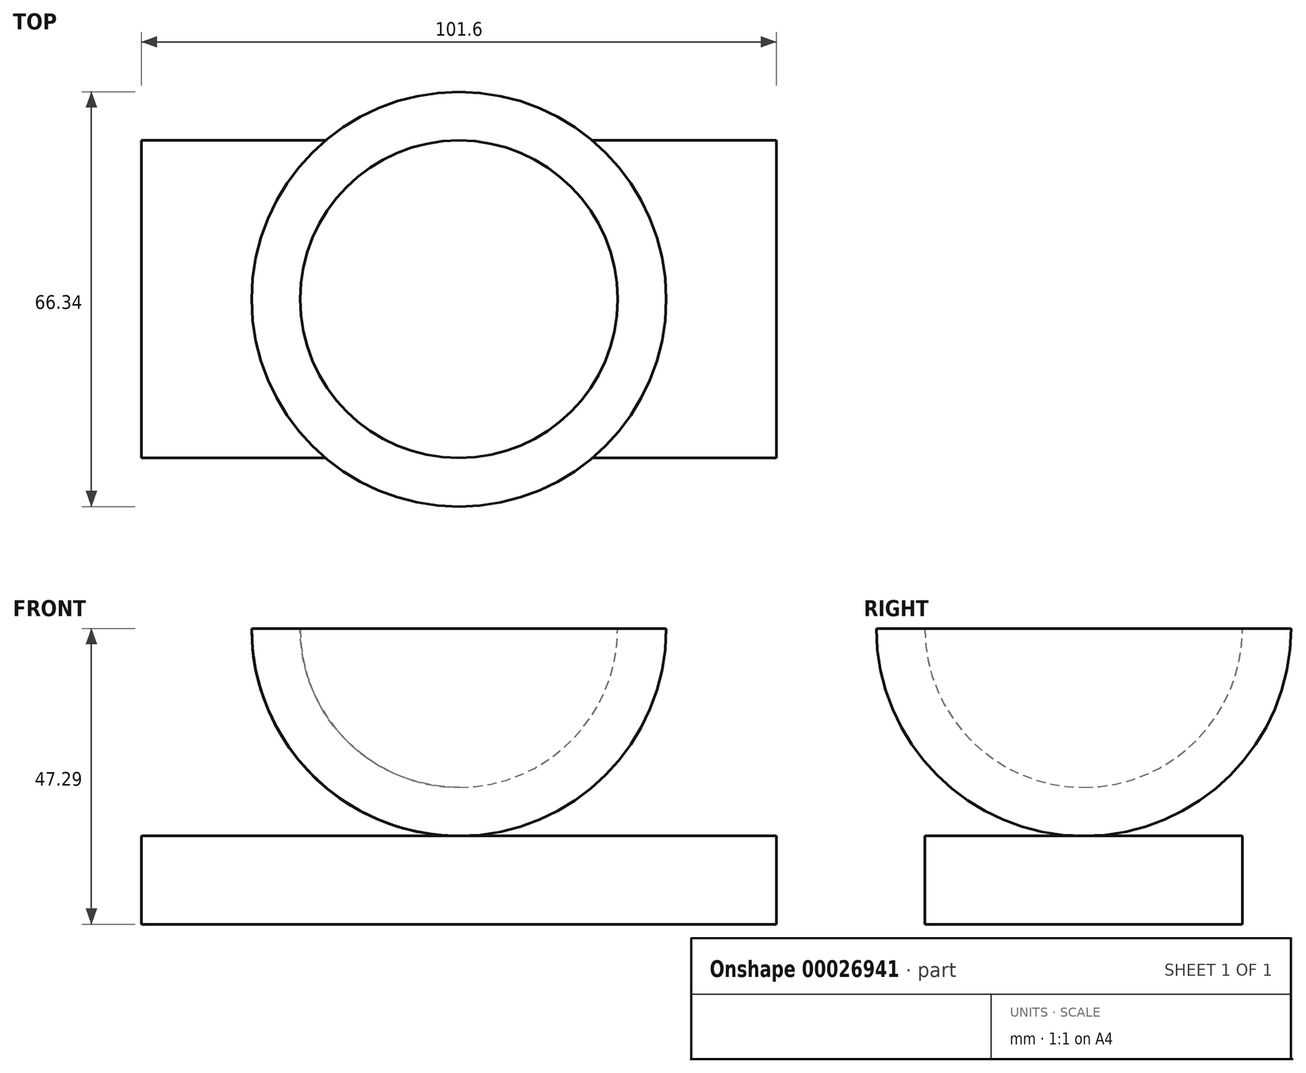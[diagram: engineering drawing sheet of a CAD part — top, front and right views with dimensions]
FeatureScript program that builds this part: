
annotation { "Feature Type Name" : "Feature", "Feature Type Description" : "" }
export const myFeature = defineFeature(function(context is Context, id is Id, definition is map)
    precondition{}
    {
        {
            var Q0;
            Q0=qCreatedBy(makeId("Front.planeOp"),FACE);
            var sketch = newSketch(context, id + "F0", { "sketchPlane" : qUnion([Q0])});
            skLineSegment(sketch, "E0", {"start": v(42.74, 22.2) * mm, "end": v(50.52, 22.2) * mm});
            skLineSegment(sketch, "E1", {"start": v(50.52, 22.2) * mm, "end": v(42.74, 22.2) * mm});
            skLineSegment(sketch, "E2", {"start": v(17.34, -10.97) * mm, "end": v(17.34, -25.09) * mm});
            skArc(sketch, "E3", {"start": v(-15.83, 22.2) * mm, "mid": v(17.34, -10.97) * mm, "end": v(50.52, 22.2) * mm});
            skArc(sketch, "E4", {"start": v(-8.06, 22.2) * mm, "mid": v(17.34, -3.2) * mm, "end": v(42.74, 22.2) * mm});
            skLineSegment(sketch, "E5.bottom", {"start": v(17.34, -25.09) * mm, "end": v(68.14, -25.09) * mm});
            skLineSegment(sketch, "E5.top", {"start": v(17.34, -10.97) * mm, "end": v(68.14, -10.97) * mm});
            skLineSegment(sketch, "E5.right", {"start": v(68.14, -10.97) * mm, "end": v(68.14, -25.09) * mm});
            skLineSegment(sketch, "E6.MirrorCS", {"start": v(17.34, -10.97) * mm, "end": v(-33.46, -10.97) * mm});
            skLineSegment(sketch, "E7.MirrorCS", {"start": v(-33.46, -10.97) * mm, "end": v(-33.46, -25.09) * mm});
            skLineSegment(sketch, "E8.MirrorCS", {"start": v(17.34, -25.09) * mm, "end": v(-33.46, -25.09) * mm});
            skLineSegment(sketch, "E9.trimOffspring", {"start": v(-8.06, 22.2) * mm, "end": v(-15.83, 22.2) * mm});
            skLineSegment(sketch, "E10", {"start": v(17.34, 22.2) * mm, "end": v(17.34, -25.09) * mm});
            skSolve(sketch);
        }
        {
            var Q0;
            {var subQ0=sQuery(id+"F0.wireOp",EDGE,"E9.trimOffspring");Q0=makeQuery(id+"F0.imprint","IMPRINT",FACE,{"disambiguationData":[TD([[makeQuery(id+"F0.imprint","IMPRINT",EDGE,{"derivedFrom":subQ0}),1.0]])]});}
            var Q1;
            {var subQ3=sQuery(id+"F0.wireOp",EDGE,"E2");Q1=makeQuery(id+"F0.imprint","IMPRINT",FACE,{"disambiguationData":[TD([[makeQuery(id+"F0.imprint","IMPRINT",EDGE,{"derivedFrom":subQ3}),-1.0]])]});}
            var Q2;
            Q2=sQuery(id+"F0.wireOp",EDGE,"E2");
            revolve(context, id + "F1", {"entities" : qUnion([Q0, Q1]), "axis" : qUnion([Q2]), "revolveType" : RevolveType.FULL});
        }
        {
            var Q0;
            {var subQ1=sQuery(id+"F0.wireOp",EDGE,"E6.MirrorCS");Q0=makeQuery(id+"F0.imprint","IMPRINT",FACE,{"disambiguationData":[TD([[makeQuery(id+"F0.imprint","IMPRINT",EDGE,{"derivedFrom":subQ1}),1.0]])]});}
            var Q1;
            {var subQ2=sQuery(id+"F0.wireOp",EDGE,"E5.bottom");Q1=makeQuery(id+"F0.imprint","IMPRINT",FACE,{"disambiguationData":[TD([[makeQuery(id+"F0.imprint","IMPRINT",EDGE,{"derivedFrom":subQ2}),1.0]])]});}
            extrude(context, id + "F2", {"entities" : qUnion([Q0, Q1]), "endBound" : BoundingType.SYMMETRIC, "depth" : 50.8 * mm});
        }
    });
